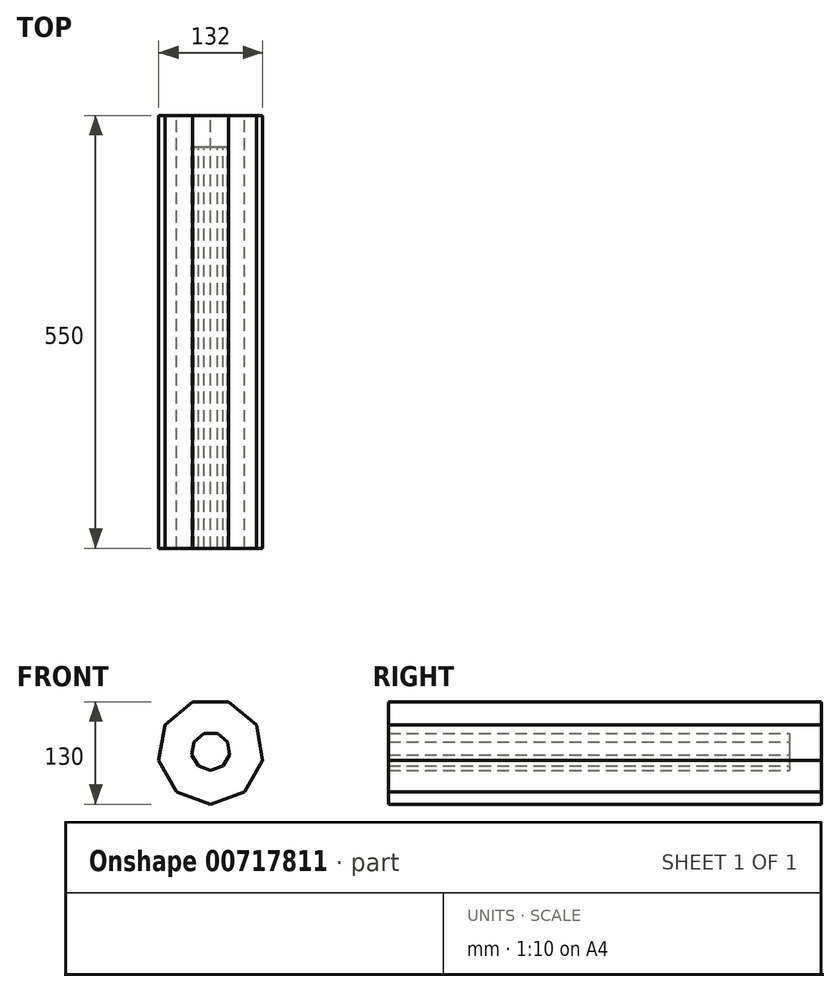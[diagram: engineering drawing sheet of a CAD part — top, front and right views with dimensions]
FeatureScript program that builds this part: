
annotation { "Feature Type Name" : "Feature", "Feature Type Description" : "" }
export const myFeature = defineFeature(function(context is Context, id is Id, definition is map)
    precondition{}
    {
        {
            var Q0;
            Q0=qCreatedBy(makeId("Front.planeOp"),FACE);
            var sketch = newSketch(context, id + "F0", { "sketchPlane" : qUnion([Q0])});
            skCircle(sketch, "E0.cCircle", {"center": v(0, 0) * mm, "radius": 62.98 * mm, "construction": true});
            skLineSegment(sketch, "E0.0", {"start": v(-22.92, 62.98) * mm, "end": v(22.92, 62.98) * mm});
            skLineSegment(sketch, "E0.1", {"start": v(22.92, 62.98) * mm, "end": v(58.04, 33.51) * mm});
            skLineSegment(sketch, "E0.2", {"start": v(58.04, 33.51) * mm, "end": v(66, -11.64) * mm});
            skLineSegment(sketch, "E0.3", {"start": v(66, -11.64) * mm, "end": v(43.08, -51.34) * mm});
            skLineSegment(sketch, "E0.4", {"start": v(43.08, -51.34) * mm, "end": v(0, -67.02) * mm});
            skLineSegment(sketch, "E0.5", {"start": v(0, -67.02) * mm, "end": v(-43.08, -51.34) * mm});
            skLineSegment(sketch, "E0.6", {"start": v(-43.08, -51.34) * mm, "end": v(-66, -11.64) * mm});
            skLineSegment(sketch, "E0.7", {"start": v(-66, -11.64) * mm, "end": v(-58.04, 33.51) * mm});
            skLineSegment(sketch, "E0.8", {"start": v(-58.04, 33.51) * mm, "end": v(-22.92, 62.98) * mm});
            skPoint(sketch, "E0.0.midPoint", {"position": v(0, 62.98) * mm});
            skSolve(sketch);
        }
        {
            var Q0;
            Q0 = qSketchRegion(id + "F0", true);
            extrude(context, id + "F1", {"entities" : qUnion([Q0]), "depth" : 550 * mm, "offsetDistance" : 25.4 * mm});
        }
        {
            var Q0;
            Q0=makeQuery(id+"F1.opExtrude","CAP_FACE",FACE,{"disambiguationData":[OSD([sQuery(id+"F0.wireOp",EDGE,"E0.0"),sQuery(id+"F0.wireOp",EDGE,"E0.1"),sQuery(id+"F0.wireOp",EDGE,"E0.2"),sQuery(id+"F0.wireOp",EDGE,"E0.3"),sQuery(id+"F0.wireOp",EDGE,"E0.4"),sQuery(id+"F0.wireOp",EDGE,"E0.5"),sQuery(id+"F0.wireOp",EDGE,"E0.6"),sQuery(id+"F0.wireOp",EDGE,"E0.7"),sQuery(id+"F0.wireOp",EDGE,"E0.8")])],"isStart":false});
            shell(context, id + "F2", {"entities" : qUnion([Q0]), "thickness" : 40 * mm});
        }
    });
